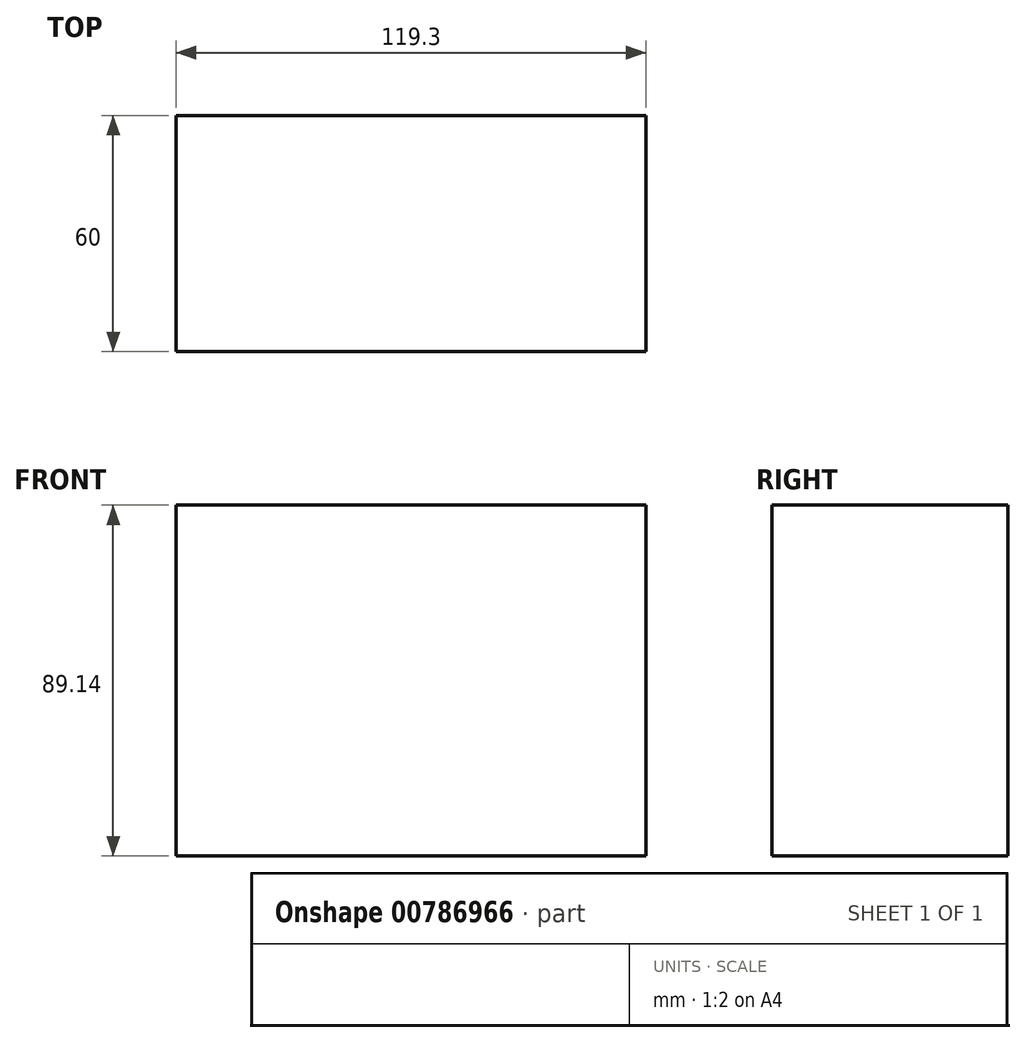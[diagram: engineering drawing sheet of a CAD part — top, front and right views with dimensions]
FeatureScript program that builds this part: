
annotation { "Feature Type Name" : "Feature", "Feature Type Description" : "" }
export const myFeature = defineFeature(function(context is Context, id is Id, definition is map)
    precondition{}
    {
        {
            var Q0;
            Q0=qCreatedBy(makeId("Front.planeOp"),FACE);
            var sketch = newSketch(context, id + "F0", { "sketchPlane" : qUnion([Q0])});
            skLineSegment(sketch, "E0.bottom", {"start": v(59.65, 44.57) * mm, "end": v(-59.65, 44.57) * mm});
            skLineSegment(sketch, "E0.top", {"start": v(59.65, -44.57) * mm, "end": v(-59.65, -44.57) * mm});
            skLineSegment(sketch, "E0.left", {"start": v(59.65, 44.57) * mm, "end": v(59.65, -44.57) * mm});
            skLineSegment(sketch, "E0.right", {"start": v(-59.65, 44.57) * mm, "end": v(-59.65, -44.57) * mm});
            skPoint(sketch, "E0.middle", {"position": v(0, 0) * mm});
            skSolve(sketch);
        }
        {
            var Q0;
            Q0 = qSketchRegion(id + "F0", true);
            extrude(context, id + "F1", {"entities" : qUnion([Q0]), "depth" : 30 * mm, "offsetDistance" : 25 * mm});
        }
        {
            var Q0;
            Q0=makeQuery(id+"F1.opExtrude","CAP_FACE",FACE,{"disambiguationData":[OSD([sQuery(id+"F0.wireOp",EDGE,"E0.bottom"),sQuery(id+"F0.wireOp",EDGE,"E0.top"),sQuery(id+"F0.wireOp",EDGE,"E0.left"),sQuery(id+"F0.wireOp",EDGE,"E0.right")])],"isStart":true});
            extrude(context, id + "F2", {"entities" : qUnion([Q0]), "operationType" : NewBodyOperationType.ADD, "depth" : 30 * mm, "offsetDistance" : 25 * mm});
        }
    });
